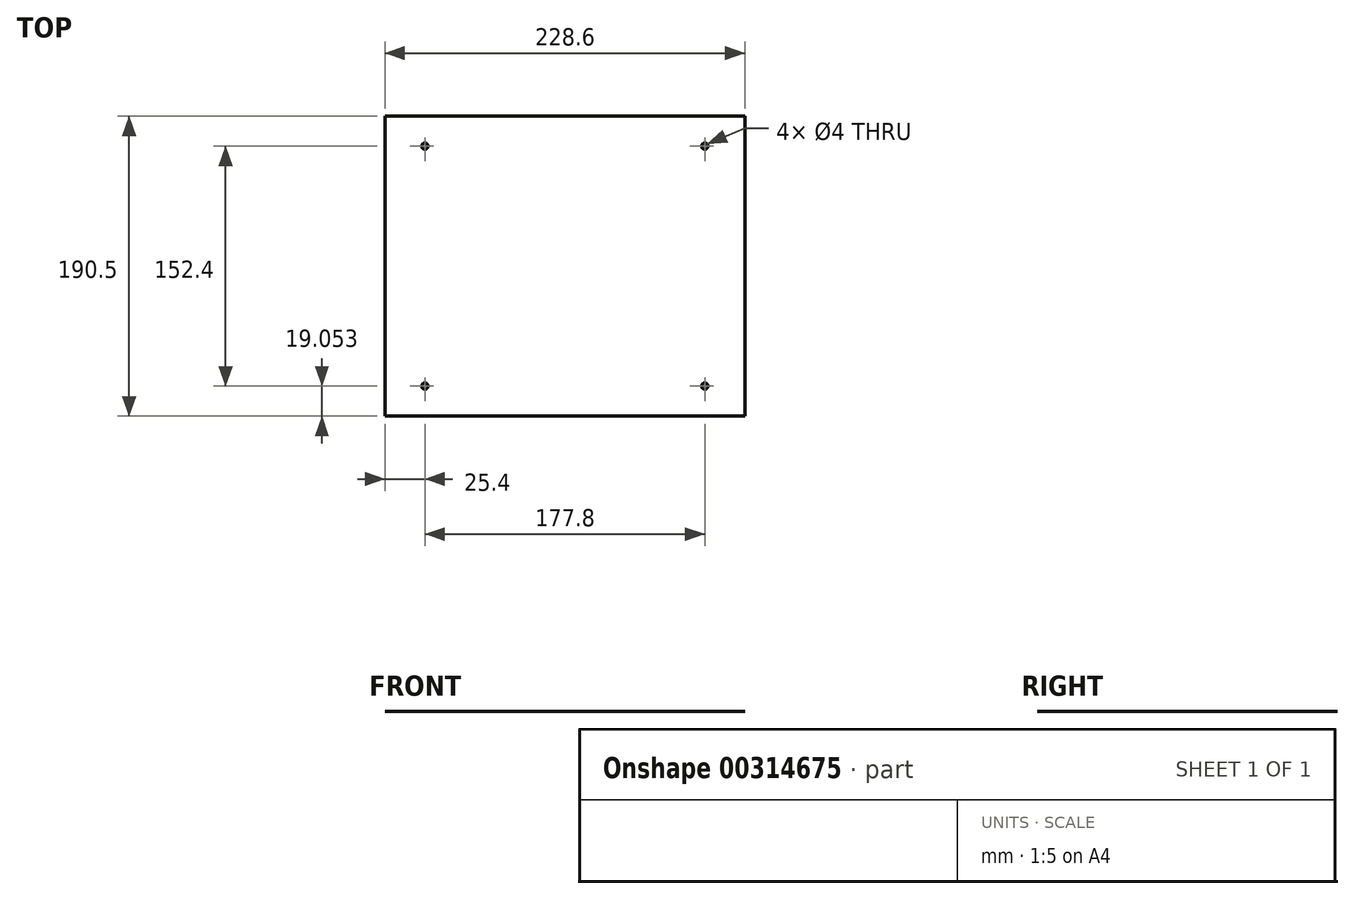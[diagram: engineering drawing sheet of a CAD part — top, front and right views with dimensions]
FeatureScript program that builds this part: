
annotation { "Feature Type Name" : "Feature", "Feature Type Description" : "" }
export const myFeature = defineFeature(function(context is Context, id is Id, definition is map)
    precondition{}
    {
        {
            var Q0;
            Q0=qCreatedBy(makeId("Top.planeOp"),FACE);
            var sketch = newSketch(context, id + "F0", { "sketchPlane" : qUnion([Q0])});
            skLineSegment(sketch, "E0.bottom", {"start": v(-379.16, -384.73) * mm, "end": v(-607.76, -384.73) * mm});
            skLineSegment(sketch, "E0.top", {"start": v(-379.16, -194.23) * mm, "end": v(-607.76, -194.23) * mm});
            skLineSegment(sketch, "E0.left", {"start": v(-379.16, -384.73) * mm, "end": v(-379.16, -194.23) * mm});
            skLineSegment(sketch, "E0.right", {"start": v(-607.76, -384.73) * mm, "end": v(-607.76, -194.23) * mm});
            skPoint(sketch, "E0.middle", {"position": v(-493.46, -289.48) * mm});
            skLineSegment(sketch, "E1.bottom", {"start": v(-582.36, -213.28) * mm, "end": v(-404.56, -213.28) * mm, "construction": true});
            skLineSegment(sketch, "E1.top", {"start": v(-582.36, -365.68) * mm, "end": v(-404.56, -365.68) * mm, "construction": true});
            skLineSegment(sketch, "E1.left", {"start": v(-582.36, -213.28) * mm, "end": v(-582.36, -365.68) * mm, "construction": true});
            skLineSegment(sketch, "E1.right", {"start": v(-404.56, -213.28) * mm, "end": v(-404.56, -365.68) * mm, "construction": true});
            skCircle(sketch, "E2", {"center": v(-582.36, -213.28) * mm, "radius": 2 * mm});
            skCircle(sketch, "E3", {"center": v(-582.36, -365.68) * mm, "radius": 2 * mm});
            skCircle(sketch, "E4", {"center": v(-404.56, -365.68) * mm, "radius": 2 * mm});
            skCircle(sketch, "E5", {"center": v(-404.56, -213.28) * mm, "radius": 2 * mm});
            skSolve(sketch);
        }
        {
            var Q0;
            Q0 = qSketchRegion(id + "F0", true);
            extrude(context, id + "F1", {"entities" : qUnion([Q0]), "depth" : 1 / 203.2 * mm});
        }
    });
